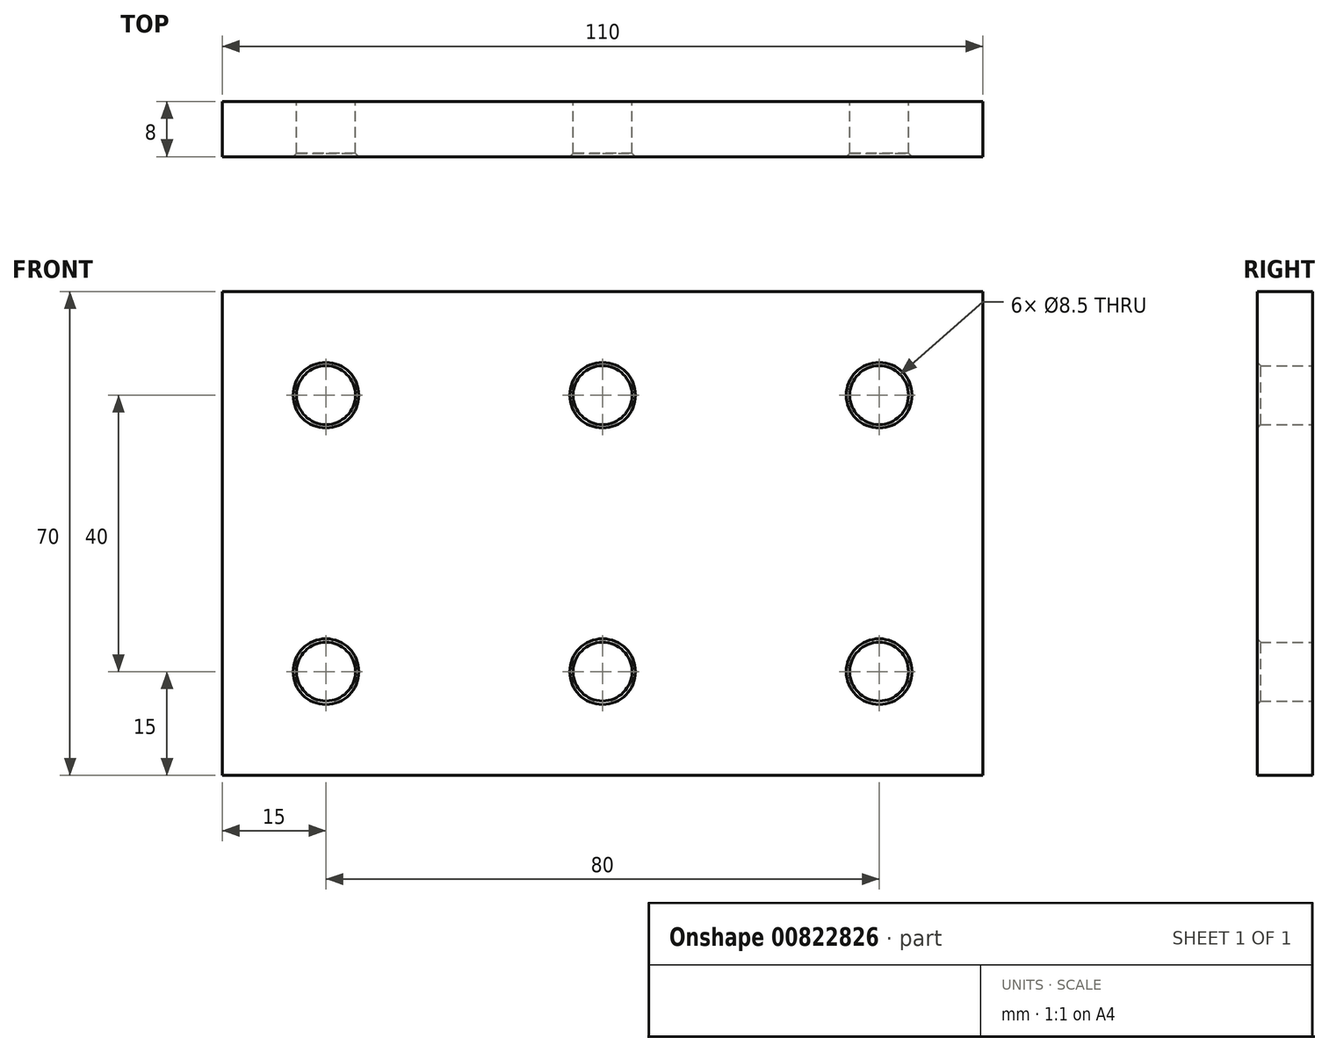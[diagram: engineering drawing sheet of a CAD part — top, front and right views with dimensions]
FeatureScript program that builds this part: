
annotation { "Feature Type Name" : "Feature", "Feature Type Description" : "" }
export const myFeature = defineFeature(function(context is Context, id is Id, definition is map)
    precondition{}
    {
        {
            var Q0;
            Q0=qCreatedBy(makeId("Front.planeOp"),FACE);
            var sketch = newSketch(context, id + "F0", { "sketchPlane" : qUnion([Q0])});
            skLineSegment(sketch, "E0.bottom", {"start": v(-55, -35) * mm, "end": v(55, -35) * mm});
            skLineSegment(sketch, "E0.top", {"start": v(-55, 35) * mm, "end": v(55, 35) * mm});
            skLineSegment(sketch, "E0.left", {"start": v(-55, -35) * mm, "end": v(-55, 35) * mm});
            skLineSegment(sketch, "E0.right", {"start": v(55, -35) * mm, "end": v(55, 35) * mm});
            skPoint(sketch, "E0.middle", {"position": v(0, 0) * mm});
            skLineSegment(sketch, "E1.bottom", {"start": v(-40, -20) * mm, "end": v(40, -20) * mm, "construction": true});
            skLineSegment(sketch, "E1.top", {"start": v(-40, 20) * mm, "end": v(40, 20) * mm, "construction": true});
            skLineSegment(sketch, "E1.left", {"start": v(-40, -20) * mm, "end": v(-40, 20) * mm, "construction": true});
            skLineSegment(sketch, "E1.right", {"start": v(40, -20) * mm, "end": v(40, 20) * mm, "construction": true});
            skCircle(sketch, "E2", {"center": v(-40, 20) * mm, "radius": 4.25 * mm});
            skCircle(sketch, "E3.0.1.0", {"center": v(-40, -20) * mm, "radius": 4.25 * mm});
            skCircle(sketch, "E3.1.0.0", {"center": v(0, 20) * mm, "radius": 4.25 * mm});
            skCircle(sketch, "E3.1.1.0", {"center": v(0, -20) * mm, "radius": 4.25 * mm});
            skCircle(sketch, "E3.2.0.0", {"center": v(40, 20) * mm, "radius": 4.25 * mm});
            skCircle(sketch, "E3.2.1.0", {"center": v(40, -20) * mm, "radius": 4.25 * mm});
            skLineSegment(sketch, "E3.direction1", {"start": v(-40, 20) * mm, "end": v(0, 20) * mm, "construction": true});
            skLineSegment(sketch, "E3.direction2", {"start": v(-40, 20) * mm, "end": v(-40, -20) * mm, "construction": true});
            skSolve(sketch);
        }
        {
            var Q0;
            Q0 = qSketchRegion(id + "F0", true);
            extrude(context, id + "F1", {"entities" : qUnion([Q0]), "depth" : 8 * mm, "offsetDistance" : 25 * mm});
        }
        {
            var Q0;
            Q0=makeQuery(id+"F1.opExtrude","CAP_EDGE",EDGE,{"disambiguationData":[OSD([sQuery(id+"F0.wireOp",EDGE,"E2")])],"isStart":false});
            var Q1;
            Q1=makeQuery(id+"F1.opExtrude","CAP_EDGE",EDGE,{"disambiguationData":[OSD([sQuery(id+"F0.wireOp",EDGE,"E3.0.1.0")])],"isStart":false});
            var Q2;
            Q2=makeQuery(id+"F1.opExtrude","CAP_EDGE",EDGE,{"disambiguationData":[OSD([sQuery(id+"F0.wireOp",EDGE,"E3.1.1.0")])],"isStart":false});
            var Q3;
            Q3=makeQuery(id+"F1.opExtrude","CAP_EDGE",EDGE,{"disambiguationData":[OSD([sQuery(id+"F0.wireOp",EDGE,"E3.1.0.0")])],"isStart":false});
            var Q4;
            Q4=makeQuery(id+"F1.opExtrude","CAP_EDGE",EDGE,{"disambiguationData":[OSD([sQuery(id+"F0.wireOp",EDGE,"E3.2.0.0")])],"isStart":false});
            var Q5;
            Q5=makeQuery(id+"F1.opExtrude","CAP_EDGE",EDGE,{"disambiguationData":[OSD([sQuery(id+"F0.wireOp",EDGE,"E3.2.1.0")])],"isStart":false});
            chamfer(context, id + "F2", {"entities" : qUnion([Q0, Q1, Q2, Q3, Q4, Q5]), "width" : 0.5 * mm, "tangentPropagation" : true});
        }
    });
